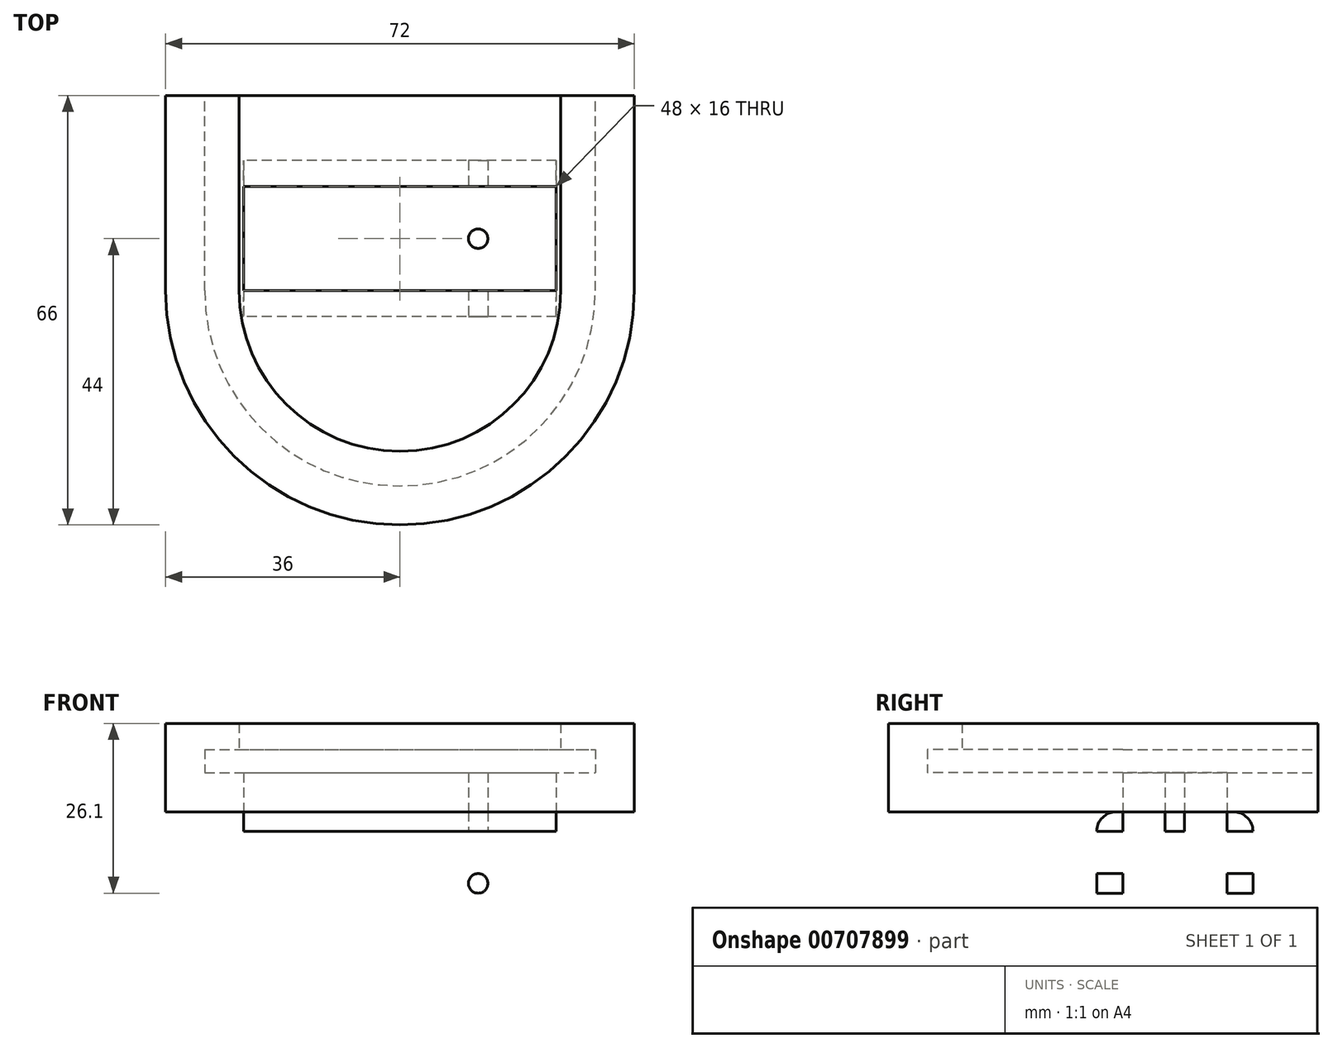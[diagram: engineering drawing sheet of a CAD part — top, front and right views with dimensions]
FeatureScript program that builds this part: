
annotation { "Feature Type Name" : "Feature", "Feature Type Description" : "" }
export const myFeature = defineFeature(function(context is Context, id is Id, definition is map)
    precondition{}
    {
        {
            var Q0;
            Q0=qCreatedBy(makeId("Top.planeOp"),FACE);
            var sketch = newSketch(context, id + "F0", { "sketchPlane" : qUnion([Q0])});
            skLineSegment(sketch, "E0", {"start": v(-30, 0) * mm, "end": v(-30, 30) * mm});
            skLineSegment(sketch, "E1.MirrorCS", {"start": v(30, 0) * mm, "end": v(30, 30) * mm});
            skArc(sketch, "E2", {"start": v(-30, 0) * mm, "mid": v(0, -30) * mm, "end": v(30, 0) * mm});
            skLineSegment(sketch, "E3.0", {"start": v(-36, 0) * mm, "end": v(-36, 30) * mm});
            skArc(sketch, "E3.1", {"start": v(-36, 0) * mm, "mid": v(0, -36) * mm, "end": v(36, 0) * mm});
            skLineSegment(sketch, "E3.2", {"start": v(36, 0) * mm, "end": v(36, 30) * mm});
            skLineSegment(sketch, "E4", {"start": v(-30, 30) * mm, "end": v(-36, 30) * mm});
            skLineSegment(sketch, "E5", {"start": v(30, 30) * mm, "end": v(36, 30) * mm});
            skSolve(sketch);
        }
        {
            var Q0;
            Q0 = qSketchRegion(id + "F0", true);
            extrude(context, id + "F1", {"entities" : qUnion([Q0]), "depth" : 3.6 * mm, "offsetDistance" : 25 * mm});
        }
        {
            var Q0;
            Q0=makeQuery(id+"F1.opExtrude","CAP_FACE",FACE,{"disambiguationData":[OSD([sQuery(id+"F0.wireOp",EDGE,"E0"),sQuery(id+"F0.wireOp",EDGE,"E1.MirrorCS"),sQuery(id+"F0.wireOp",EDGE,"E2"),sQuery(id+"F0.wireOp",EDGE,"E3.0"),sQuery(id+"F0.wireOp",EDGE,"E3.1"),sQuery(id+"F0.wireOp",EDGE,"E3.2"),sQuery(id+"F0.wireOp",EDGE,"E4"),sQuery(id+"F0.wireOp",EDGE,"E5")])],"isStart":false});
            var sketch = newSketch(context, id + "F2", { "sketchPlane" : qUnion([Q0])});
            skLineSegment(sketch, "E6.0", {"start": v(-30, 0) * mm, "end": v(-30, 30) * mm});
            skArc(sketch, "E6.1", {"start": v(-30, 0) * mm, "mid": v(0, -30) * mm, "end": v(30, 0) * mm});
            skLineSegment(sketch, "E6.2", {"start": v(30, 0) * mm, "end": v(30, 30) * mm});
            skLineSegment(sketch, "E6.3", {"start": v(36, 0) * mm, "end": v(36, 30) * mm});
            skArc(sketch, "E6.4", {"start": v(-36, 0) * mm, "mid": v(0, -36) * mm, "end": v(36, 0) * mm});
            skLineSegment(sketch, "E6.5", {"start": v(-36, 0) * mm, "end": v(-36, 30) * mm});
            skLineSegment(sketch, "E6.6", {"start": v(-30, 30) * mm, "end": v(-36, 30) * mm});
            skLineSegment(sketch, "E6.7", {"start": v(30, 30) * mm, "end": v(36, 30) * mm});
            skLineSegment(sketch, "E7.0", {"start": v(-24.7, 0) * mm, "end": v(-24.7, 30) * mm});
            skArc(sketch, "E7.1", {"start": v(-24.7, 0) * mm, "mid": v(0, -24.7) * mm, "end": v(24.7, 0) * mm});
            skLineSegment(sketch, "E7.2", {"start": v(24.7, 0) * mm, "end": v(24.7, 30) * mm});
            skLineSegment(sketch, "E8", {"start": v(-36, 30) * mm, "end": v(-24.7, 30) * mm});
            skLineSegment(sketch, "E9", {"start": v(24.7, 30) * mm, "end": v(36, 30) * mm});
            skSolve(sketch);
        }
        {
            var Q0;
            {var subQ2=sQuery(id+"F2.wireOp",EDGE,"E6.0");Q0=makeQuery(id+"F2.imprint","IMPRINT",FACE,{"disambiguationData":[TD([[makeQuery(id+"F2.imprint","IMPRINT",EDGE,{"derivedFrom":subQ2}),-1.0]])]});}
            var Q1;
            {var subQ3=sQuery(id+"F2.wireOp",EDGE,"E6.0");Q1=makeQuery(id+"F2.imprint","IMPRINT",FACE,{"disambiguationData":[TD([[makeQuery(id+"F2.imprint","IMPRINT",EDGE,{"derivedFrom":subQ3}),1.0]])]});}
            extrude(context, id + "F3", {"entities" : qUnion([Q0, Q1]), "operationType" : NewBodyOperationType.ADD, "depth" : 4 * mm, "offsetDistance" : 25 * mm});
        }
        {
            var Q0;
            Q0=makeQuery(id+"F1.opExtrude","CAP_FACE",FACE,{"disambiguationData":[OSD([sQuery(id+"F0.wireOp",EDGE,"E0"),sQuery(id+"F0.wireOp",EDGE,"E1.MirrorCS"),sQuery(id+"F0.wireOp",EDGE,"E2"),sQuery(id+"F0.wireOp",EDGE,"E3.0"),sQuery(id+"F0.wireOp",EDGE,"E3.1"),sQuery(id+"F0.wireOp",EDGE,"E3.2"),sQuery(id+"F0.wireOp",EDGE,"E4"),sQuery(id+"F0.wireOp",EDGE,"E5")])],"isStart":true});
            var sketch = newSketch(context, id + "F4", { "sketchPlane" : qUnion([Q0])});
            skArc(sketch, "E10.0", {"start": v(-36, 0) * mm, "mid": v(0, 36) * mm, "end": v(36, 0) * mm});
            skLineSegment(sketch, "E10.1", {"start": v(-36, 0) * mm, "end": v(-36, -30) * mm});
            skLineSegment(sketch, "E10.2", {"start": v(-30, -30) * mm, "end": v(-36, -30) * mm});
            skLineSegment(sketch, "E10.3", {"start": v(30, -30) * mm, "end": v(36, -30) * mm});
            skLineSegment(sketch, "E10.4", {"start": v(36, 0) * mm, "end": v(36, -30) * mm});
            skLineSegment(sketch, "E11", {"start": v(-36, -30) * mm, "end": v(36, -30) * mm});
            skSolve(sketch);
        }
        {
            var Q0;
            Q0 = qSketchRegion(id + "F4", true);
            extrude(context, id + "F5", {"entities" : qUnion([Q0]), "operationType" : NewBodyOperationType.ADD, "depth" : 6 * mm, "offsetDistance" : 25 * mm});
        }
        {
            var Q0;
            Q0=makeQuery(id+"F5.opExtrude","CAP_FACE",FACE,{"disambiguationData":[OSD([sQuery(id+"F4.wireOp",EDGE,"E10.0"),sQuery(id+"F4.wireOp",EDGE,"E10.1"),sQuery(id+"F4.wireOp",EDGE,"E10.4"),sQuery(id+"F4.wireOp",EDGE,"E11")])],"isStart":false});
            var sketch = newSketch(context, id + "F6", { "sketchPlane" : qUnion([Q0])});
            skArc(sketch, "E12.0", {"start": v(-36, 0) * mm, "mid": v(0, 36) * mm, "end": v(36, 0) * mm});
            skLineSegment(sketch, "E12.1", {"start": v(-36, 0) * mm, "end": v(-36, -30) * mm});
            skLineSegment(sketch, "E12.2", {"start": v(-36, -30) * mm, "end": v(36, -30) * mm});
            skLineSegment(sketch, "E12.3", {"start": v(36, 0) * mm, "end": v(36, -30) * mm});
            skLineSegment(sketch, "E13.bottom", {"start": v(24, -20) * mm, "end": v(12, -20) * mm});
            skLineSegment(sketch, "E13.top", {"start": v(24, 4) * mm, "end": v(12, 4) * mm});
            skLineSegment(sketch, "E13.left", {"start": v(24, -20) * mm, "end": v(24, 4) * mm});
            skLineSegment(sketch, "E13.right", {"start": v(12, -20) * mm, "end": v(12, 4) * mm});
            skLineSegment(sketch, "E14.MirrorCS", {"start": v(-12, -20) * mm, "end": v(-12, 4) * mm});
            skLineSegment(sketch, "E15.MirrorCS", {"start": v(-24, 4) * mm, "end": v(-12, 4) * mm});
            skLineSegment(sketch, "E16.MirrorCS", {"start": v(-24, -20) * mm, "end": v(-24, 4) * mm});
            skLineSegment(sketch, "E17.MirrorCS", {"start": v(-24, -20) * mm, "end": v(-12, -20) * mm});
            skLineSegment(sketch, "E18", {"start": v(-12, 4) * mm, "end": v(12, 4) * mm});
            skLineSegment(sketch, "E19", {"start": v(-12, -20) * mm, "end": v(12, -20) * mm});
            skSolve(sketch);
        }
        {
            var Q0;
            Q0=makeQuery(id+"F6.imprint","IMPRINT",FACE,{"disambiguationData":[TD([[makeQuery(id+"F6.imprint","IMPRINT",EDGE,{"derivedFrom":sQuery(id+"F6.wireOp",EDGE,"E13.bottom")}),-1.0]])]});
            var Q1;
            Q1=makeQuery(id+"F6.imprint","IMPRINT",FACE,{"disambiguationData":[TD([[makeQuery(id+"F6.imprint","IMPRINT",EDGE,{"derivedFrom":sQuery(id+"F6.wireOp",EDGE,"E14.MirrorCS")}),1.0]])]});
            var Q2;
            Q2=makeQuery(id+"F6.imprint","IMPRINT",FACE,{"disambiguationData":[TD([[makeQuery(id+"F6.imprint","IMPRINT",EDGE,{"derivedFrom":sQuery(id+"F6.wireOp",EDGE,"E13.right")}),1.0]])]});
            extrude(context, id + "F7", {"entities" : qUnion([Q0, Q1, Q2]), "depth" : 4 * mm, "offsetDistance" : 25 * mm});
        }
        {
            var Q0;
            Q0=makeQuery(id+"F7.opExtrude","CAP_FACE",FACE,{"disambiguationData":[OSD([sQuery(id+"F6.wireOp",EDGE,"E13.bottom"),sQuery(id+"F6.wireOp",EDGE,"E13.top"),sQuery(id+"F6.wireOp",EDGE,"E13.left"),sQuery(id+"F6.wireOp",EDGE,"E15.MirrorCS"),sQuery(id+"F6.wireOp",EDGE,"E16.MirrorCS"),sQuery(id+"F6.wireOp",EDGE,"E17.MirrorCS"),sQuery(id+"F6.wireOp",EDGE,"E18"),sQuery(id+"F6.wireOp",EDGE,"E19")])],"isStart":false});
            var sketch = newSketch(context, id + "F8", { "sketchPlane" : qUnion([Q0])});
            skLineSegment(sketch, "E20", {"start": v(-24, -8) * mm, "end": v(24, -8) * mm, "construction": true});
            skLineSegment(sketch, "E21", {"start": v(-24, 0) * mm, "end": v(24, 0) * mm});
            skLineSegment(sketch, "E22.MirrorCS", {"start": v(-24, -16) * mm, "end": v(24, -16) * mm});
            skSolve(sketch);
        }
        {
            var Q0;
            Q0 = qSketchRegion(id + "F8", true);
            var Q1;
            {var subQ0=sQuery(id+"F8.wireOp",EDGE,"E21");Q1=makeQuery(id+"F8.imprint","IMPRINT",FACE,{"disambiguationData":[TD([[makeQuery(id+"F8.imprint","IMPRINT",EDGE,{"derivedFrom":subQ0}),1.0]])]});}
            var Q2;
            {var subQ0=sQuery(id+"F8.wireOp",EDGE,"E22.MirrorCS");Q2=makeQuery(id+"F8.imprint","IMPRINT",FACE,{"disambiguationData":[TD([[makeQuery(id+"F8.imprint","IMPRINT",EDGE,{"derivedFrom":subQ0}),-1.0]])]});}
            extrude(context, id + "F9", {"entities" : qUnion([Q0, Q1, Q2]), "operationType" : NewBodyOperationType.ADD, "depth" : 15 * mm, "offsetDistance" : 25 * mm});
        }
        {
            var Q0;
            Q0=makeQuery(id+"F7.opExtrude","CAP_FACE",FACE,{"disambiguationData":[OSD([sQuery(id+"F6.wireOp",EDGE,"E13.bottom"),sQuery(id+"F6.wireOp",EDGE,"E13.top"),sQuery(id+"F6.wireOp",EDGE,"E13.left"),sQuery(id+"F6.wireOp",EDGE,"E15.MirrorCS"),sQuery(id+"F6.wireOp",EDGE,"E16.MirrorCS"),sQuery(id+"F6.wireOp",EDGE,"E17.MirrorCS"),sQuery(id+"F6.wireOp",EDGE,"E18"),sQuery(id+"F6.wireOp",EDGE,"E19")])],"isStart":false});
            var sketch = newSketch(context, id + "F10", { "sketchPlane" : qUnion([Q0])});
            skLineSegment(sketch, "E23", {"start": v(-24, -8) * mm, "end": v(24, -8) * mm, "construction": true});
            skCircle(sketch, "E24", {"center": v(-12, -8) * mm, "radius": 1.5 * mm});
            skCircle(sketch, "E25.MirrorC", {"center": v(12, -8) * mm, "radius": 1.5 * mm});
            skSolve(sketch);
        }
        {
            var Q0;
            Q0=makeQuery(id+"F10.imprint","IMPRINT",FACE,{"disambiguationData":[TD([[makeQuery(id+"F10.imprint","IMPRINT",EDGE,{"derivedFrom":sQuery(id+"F10.wireOp",EDGE,"E25.MirrorC")}),-1.0]])]});
            var Q1;
            Q1=makeQuery(id+"F10.imprint","IMPRINT",FACE,{"disambiguationData":[TD([[makeQuery(id+"F10.imprint","IMPRINT",EDGE,{"derivedFrom":sQuery(id+"F10.wireOp",EDGE,"E24")}),1.0]])]});
            extrude(context, id + "F11", {"entities" : qUnion([Q0, Q1]), "operationType" : NewBodyOperationType.REMOVE, "oppositeDirection" : true, "depth" : 10 * mm, "offsetDistance" : 25 * mm});
        }
        {
            var Q0;
            Q0=makeQuery(id+"F5.opExtrude","CAP_FACE",FACE,{"disambiguationData":[OSD([sQuery(id+"F4.wireOp",EDGE,"E10.0"),sQuery(id+"F4.wireOp",EDGE,"E10.1"),sQuery(id+"F4.wireOp",EDGE,"E10.4"),sQuery(id+"F4.wireOp",EDGE,"E11")])],"isStart":true});
            var sketch = newSketch(context, id + "F12", { "sketchPlane" : qUnion([Q0])});
            skCircle(sketch, "E26.0", {"center": v(12, 8) * mm, "radius": 1.5 * mm});
            skCircle(sketch, "E26.1", {"center": v(-12, 8) * mm, "radius": 1.5 * mm});
            skCircle(sketch, "E27", {"center": v(-12, 8) * mm, "radius": 4 * mm});
            skCircle(sketch, "E28.MirrorC", {"center": v(12, 8) * mm, "radius": 4 * mm});
            skSolve(sketch);
        }
        {
            var Q0;
            Q0 = qSketchRegion(id + "F12", true);
            extrude(context, id + "F13", {"entities" : qUnion([Q0]), "operationType" : NewBodyOperationType.REMOVE, "oppositeDirection" : true, "depth" : 2 * mm, "offsetDistance" : 25 * mm});
        }
        {
            var Q0;
            Q0=makeQuery(id+"F9.opExtrude","CAP_EDGE",EDGE,{"disambiguationData":[OSD([sQuery(id+"F8.wireOp",EDGE,"E21")])],"isStart":true});
            var Q1;
            Q1=makeQuery(id+"F9.opExtrude","CAP_EDGE",EDGE,{"disambiguationData":[OSD([sQuery(id+"F8.wireOp",EDGE,"E22.MirrorCS")])],"isStart":true});
            var Q2;
            Q2=makeQuery(id+"F7.opExtrude","CAP_EDGE",EDGE,{"disambiguationData":[OSD([sQuery(id+"F6.wireOp",EDGE,"E13.top"),sQuery(id+"F6.wireOp",EDGE,"E15.MirrorCS"),sQuery(id+"F6.wireOp",EDGE,"E18")])],"isStart":true});
            var Q3;
            Q3=makeQuery(id+"F7.opExtrude","CAP_EDGE",EDGE,{"disambiguationData":[OSD([sQuery(id+"F6.wireOp",EDGE,"E13.bottom"),sQuery(id+"F6.wireOp",EDGE,"E17.MirrorCS"),sQuery(id+"F6.wireOp",EDGE,"E19")])],"isStart":true});
            fillet(context, id + "F14", {"entities" : qUnion([Q0, Q1, Q2, Q3]), "radius" : 3 * mm, "tangentPropagation" : true, "allowEdgeOverflow" : false});
        }
        {
            var Q0;
            {var subQ0=sQuery(id+"F6.wireOp",EDGE,"E18");var subQ1=sQuery(id+"F6.wireOp",EDGE,"E15.MirrorCS");var subQ2=sQuery(id+"F6.wireOp",EDGE,"E13.top");Q0=makeQuery(id+"F9.boolean.opBoolean","MERGE",FACE,{"derivedFrom":[makeQuery(id+"F7.opExtrude","SWEPT_FACE",FACE,{"disambiguationData":[OSD([subQ2,subQ1,subQ0])]}),makeQuery(id+"F9.opExtrude","SWEPT_FACE",FACE,{"disambiguationData":[OSD([subQ2,subQ1,subQ0])]})]});}
            var sketch = newSketch(context, id + "F15", { "sketchPlane" : qUnion([Q0])});
            skLineSegment(sketch, "E29.0", {"start": v(24, -9) * mm, "end": v(-24, -9) * mm});
            skLineSegment(sketch, "E29.1", {"start": v(-24, -25) * mm, "end": v(-24, -9) * mm});
            skLineSegment(sketch, "E29.2", {"start": v(24, -25) * mm, "end": v(-24, -25) * mm});
            skLineSegment(sketch, "E29.3", {"start": v(24, -25) * mm, "end": v(24, -9) * mm});
            skCircle(sketch, "E30", {"center": v(-12, -17) * mm, "radius": 1.5 * mm});
            skLineSegment(sketch, "E31", {"start": v(-24, -17) * mm, "end": v(24, -17) * mm, "construction": true});
            skCircle(sketch, "E32.MirrorC", {"center": v(12, -17) * mm, "radius": 1.5 * mm});
            skSolve(sketch);
        }
        {
            var Q0;
            Q0=makeQuery(id+"F15.imprint","IMPRINT",FACE,{"disambiguationData":[TD([[makeQuery(id+"F15.imprint","IMPRINT",EDGE,{"derivedFrom":sQuery(id+"F15.wireOp",EDGE,"E30")}),1.0]])]});
            var Q1;
            Q1=makeQuery(id+"F15.imprint","IMPRINT",FACE,{"disambiguationData":[TD([[makeQuery(id+"F15.imprint","IMPRINT",EDGE,{"derivedFrom":sQuery(id+"F15.wireOp",EDGE,"E32.MirrorC")}),-1.0]])]});
            extrude(context, id + "F16", {"entities" : qUnion([Q0, Q1]), "operationType" : NewBodyOperationType.REMOVE, "endBound" : BoundingType.THROUGH_ALL, "oppositeDirection" : true, "depth" : 25 * mm, "offsetDistance" : 25 * mm});
        }
    });
